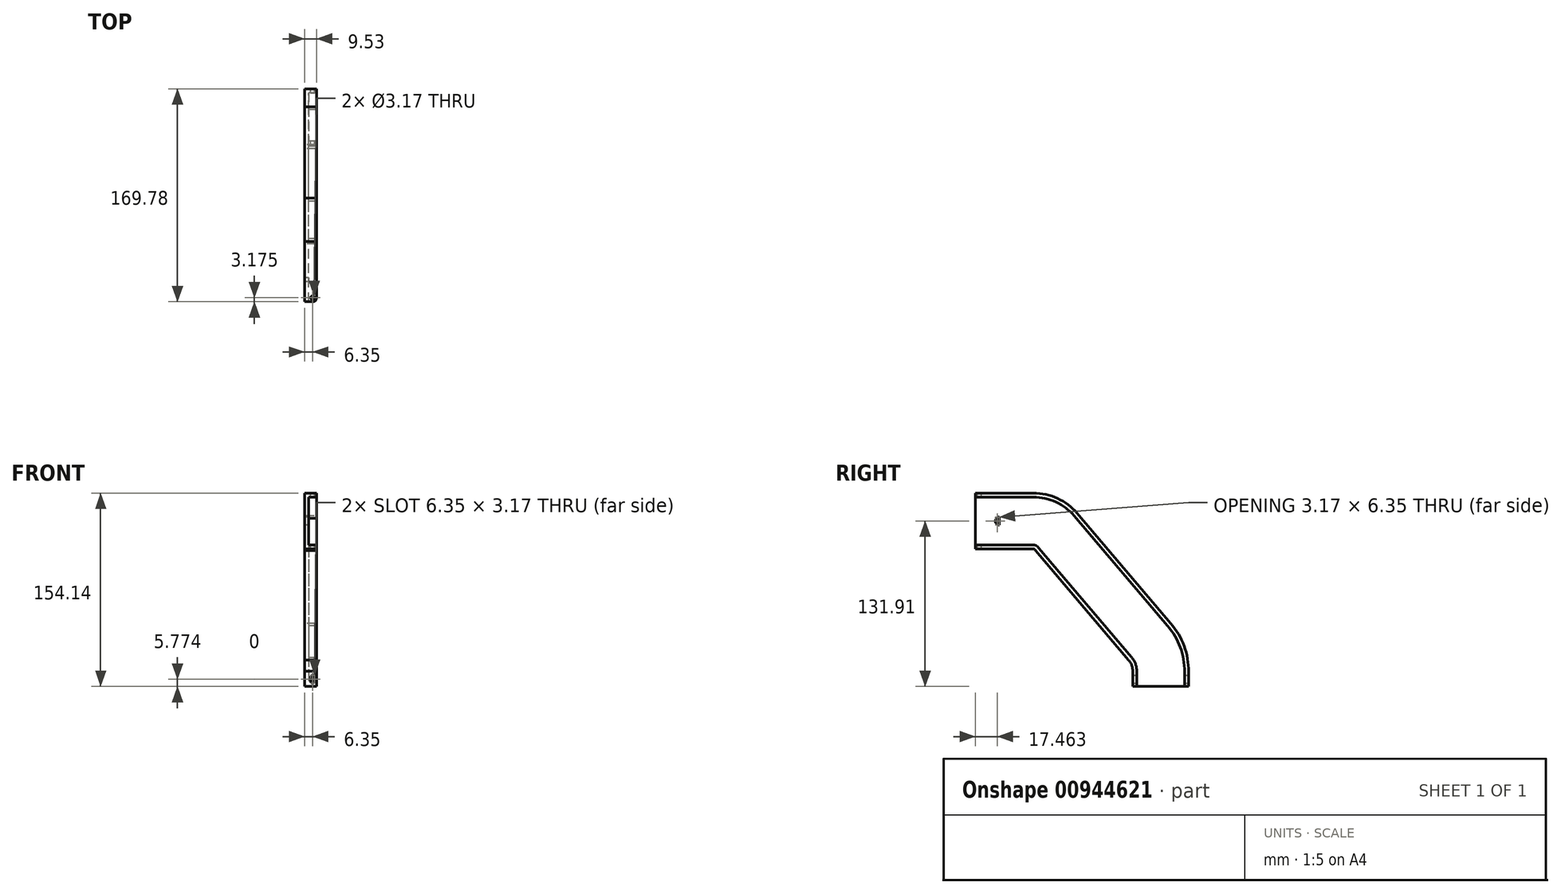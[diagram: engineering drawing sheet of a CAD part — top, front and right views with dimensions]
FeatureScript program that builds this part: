
annotation { "Feature Type Name" : "Feature", "Feature Type Description" : "" }
export const myFeature = defineFeature(function(context is Context, id is Id, definition is map)
    precondition{}
    {
        {
            var Q0;
            Q0=qCreatedBy(makeId("Front.planeOp"),FACE);
            var sketch = newSketch(context, id + "F0", { "sketchPlane" : qUnion([Q0])});
            skLineSegment(sketch, "E0.bottom", {"start": v(-3.18, 19.05) * mm, "end": v(3.18, 19.05) * mm});
            skLineSegment(sketch, "E0.top", {"start": v(-3.18, -19.05) * mm, "end": v(3.17, -19.05) * mm});
            skLineSegment(sketch, "E0.left", {"start": v(-3.18, 19.05) * mm, "end": v(-3.18, -19.05) * mm});
            skPoint(sketch, "E0.middle", {"position": v(0, 0) * mm});
            skLineSegment(sketch, "E1.0", {"start": v(-6.35, -22.22) * mm, "end": v(3.17, -22.22) * mm});
            skLineSegment(sketch, "E1.1", {"start": v(-6.35, 22.23) * mm, "end": v(-6.35, -22.23) * mm});
            skLineSegment(sketch, "E1.2", {"start": v(-6.35, 22.23) * mm, "end": v(3.18, 22.23) * mm});
            skLineSegment(sketch, "E2", {"start": v(3.18, 19.05) * mm, "end": v(3.18, 22.23) * mm});
            skLineSegment(sketch, "E3", {"start": v(3.17, -22.22) * mm, "end": v(3.17, -19.05) * mm});
            skSolve(sketch);
        }
        {
            var Q0;
            Q0 = qSketchRegion(id + "F0", true);
            extrude(context, id + "F1", {"entities" : qUnion([Q0]), "endBound" : BoundingType.SYMMETRIC, "depth" : 38.1 * mm, "offsetDistance" : 25.4 * mm});
        }
        {
            var Q0;
            Q0=makeQuery(id+"F1.opExtrude","SWEPT_FACE",FACE,{"disambiguationData":[OSD([sQuery(id+"F0.wireOp",EDGE,"E0.bottom")])]});
            var sketch = newSketch(context, id + "F2", { "sketchPlane" : qUnion([Q0])});
            skCircle(sketch, "E4", {"center": v(0, 15.88) * mm, "radius": 1.59 * mm});
            skPoint(sketch, "E4.centerSnap0", {"position": v(0, 19.05) * mm});
            skArc(sketch, "E5", {"start": v(3.18, 15.88) * mm, "mid": v(2.25, 18.12) * mm, "end": v(0, 19.05) * mm});
            skLineSegment(sketch, "E6", {"start": v(0, 19.05) * mm, "end": v(3.18, 19.05) * mm});
            skLineSegment(sketch, "E7", {"start": v(3.18, 15.88) * mm, "end": v(3.18, 19.05) * mm});
            skSolve(sketch);
        }
        {
            var Q0;
            Q0 = qSketchRegion(id + "F2", true);
            extrude(context, id + "F3", {"entities" : qUnion([Q0]), "operationType" : NewBodyOperationType.REMOVE, "endBound" : BoundingType.SYMMETRIC, "depth" : 209.9 * mm, "offsetDistance" : 25.4 * mm});
        }
        {
            var Q0;
            Q0=makeQuery(id+"F1.opExtrude","SWEPT_FACE",FACE,{"disambiguationData":[OSD([sQuery(id+"F0.wireOp",EDGE,"E1.1")])]});
            var sketch = newSketch(context, id + "F4", { "sketchPlane" : qUnion([Q0])});
            skPoint(sketch, "E8", {"position": v(0, 0) * mm});
            skSolve(sketch);
        }
        {
            var Q0;
            Q0=sQuery(id+"F4.wireOp",VERTEX,"E8");
            var Q1;
            Q1=makeQuery(id+"F1.opExtrude","SWEPT_BODY",BODY,{"disambiguationData":[OSD([sQuery(id+"F0.wireOp",EDGE,"E0.bottom"),sQuery(id+"F0.wireOp",EDGE,"E0.top"),sQuery(id+"F0.wireOp",EDGE,"E0.left"),sQuery(id+"F0.wireOp",EDGE,"E1.0"),sQuery(id+"F0.wireOp",EDGE,"E1.1"),sQuery(id+"F0.wireOp",EDGE,"E1.2"),sQuery(id+"F0.wireOp",EDGE,"E2"),sQuery(id+"F0.wireOp",EDGE,"E3")])]});
            hole(context, id + "F5", {"style" : HoleStyle.SIMPLE, "endStyle" : HoleEndStyle.BLIND, "holeDiameter" : 6.35 * mm, "majorDiameter" : 6.35 * mm, "holeDepth" : 12.7 * mm, "isTappedThrough" : true, "tappedDepth" : 12.7 * mm, "tapClearance" : 3, "startFromSketch" : true, "locations" : qUnion([Q0]), "scope" : qUnion([Q1])});
        }
        {
            var Q0;
            Q0=qCreatedBy(makeId("Right.planeOp"),FACE);
            var sketch = newSketch(context, id + "F6", { "sketchPlane" : qUnion([Q0])});
            skLineSegment(sketch, "E9.bottom", {"start": v(152.4, -114.3) * mm, "end": v(-152.4, -114.3) * mm});
            skLineSegment(sketch, "E9.top", {"start": v(152.4, 114.3) * mm, "end": v(-152.4, 114.3) * mm});
            skLineSegment(sketch, "E9.left", {"start": v(152.4, -114.3) * mm, "end": v(152.4, 114.3) * mm});
            skLineSegment(sketch, "E9.right", {"start": v(-152.4, -114.3) * mm, "end": v(-152.4, 114.3) * mm});
            skPoint(sketch, "E9.middle", {"position": v(0, 0) * mm});
            skSolve(sketch);
        }
        {
            var Q0;
            Q0=makeQuery(id+"F6.imprint","IMPRINT",FACE,{"disambiguationData":[TD([[makeQuery(id+"F6.imprint","IMPRINT",EDGE,{"derivedFrom":sQuery(id+"F6.wireOp",EDGE,"E9.bottom")}),-1.0]])]});
            var sketch = newSketch(context, id + "F7", { "sketchPlane" : qUnion([Q0])});
            skLineSegment(sketch, "E10", {"start": v(0, 0) * mm, "end": v(28.3, 0) * mm});
            skLineSegment(sketch, "E11", {"start": v(128.5, -120.1) * mm, "end": v(128.5, -131.91) * mm});
            skLineSegment(sketch, "E12", {"start": v(46.32, -9.68) * mm, "end": v(119.7, -96.15) * mm});
            skArc(sketch, "E13", {"start": v(46.32, -9.68) * mm, "mid": v(38.38, -2.86) * mm, "end": v(28.3, 0) * mm});
            skArc(sketch, "E14", {"start": v(128.5, -120.1) * mm, "mid": v(126.39, -107.29) * mm, "end": v(119.7, -96.15) * mm});
            skPoint(sketch, "E15.center.orphan", {"position": v(128.5, -106.51) * mm});
            skPoint(sketch, "E16.trimOffspring.start.orphan", {"position": v(128.5, -119.21) * mm});
            skSolve(sketch);
        }
        {
            var Q0;
            Q0=makeQuery(id+"F1.opExtrude","CAP_FACE",FACE,{"disambiguationData":[OSD([sQuery(id+"F0.wireOp",EDGE,"E0.bottom"),sQuery(id+"F0.wireOp",EDGE,"E0.top"),sQuery(id+"F0.wireOp",EDGE,"E0.left"),sQuery(id+"F0.wireOp",EDGE,"E1.0"),sQuery(id+"F0.wireOp",EDGE,"E1.1"),sQuery(id+"F0.wireOp",EDGE,"E1.2"),sQuery(id+"F0.wireOp",EDGE,"E2"),sQuery(id+"F0.wireOp",EDGE,"E3")])],"isStart":true});
            var Q1;
            Q1=sQuery(id+"F7.wireOp",EDGE,"E12");
            var Q2;
            Q2=sQuery(id+"F7.wireOp",EDGE,"E13");
            var Q3;
            Q3=sQuery(id+"F7.wireOp",EDGE,"E10");
            var Q4;
            Q4=sQuery(id+"F7.wireOp",EDGE,"E14");
            var Q5;
            Q5=sQuery(id+"F7.wireOp",EDGE,"E11");
            sweep(context, id + "F8", {"operationType" : NewBodyOperationType.ADD, "profiles" : qUnion([Q0]), "path" : qUnion([Q1, Q2, Q3, Q4, Q5])});
        }
        {
            var Q0;
            Q0=makeQuery(id+"F8.opSweep","SWEPT_FACE",FACE,{"disambiguationData":[OSD([sQuery(id+"F0.wireOp",EDGE,"E1.2"),sQuery(id+"F7.wireOp",EDGE,"E11")])]});
            var sketch = newSketch(context, id + "F9", { "sketchPlane" : qUnion([Q0])});
            skLineSegment(sketch, "E17.left", {"start": v(3.17, -127.72) * mm, "end": v(3.18, -124.55) * mm, "construction": true});
            skLineSegment(sketch, "E17.right", {"start": v(0, -127.72) * mm, "end": v(0, -124.55) * mm, "construction": true});
            skPoint(sketch, "E17.middle", {"position": v(1.59, -126.14) * mm});
            skPoint(sketch, "E17.middle.positionSnap0", {"position": v(-3.18, -126.14) * mm});
            skPoint(sketch, "E17.middle.positionSnap1", {"position": v(1.59, -131.91) * mm});
            skPoint(sketch, "E17.centerSnap0", {"position": v(-3.18, -126.14) * mm});
            skPoint(sketch, "E17.centerSnap1", {"position": v(1.59, -131.91) * mm});
            skArc(sketch, "E18", {"start": v(0, -127.72) * mm, "mid": v(1.59, -129.31) * mm, "end": v(3.17, -127.72) * mm, "construction": true});
            skArc(sketch, "E19", {"start": v(3.17, -124.55) * mm, "mid": v(1.59, -122.96) * mm, "end": v(0, -124.55) * mm, "construction": true});
            skArc(sketch, "E20", {"start": v(-1.59, -127.72) * mm, "mid": v(0, -129.31) * mm, "end": v(1.59, -127.72) * mm});
            skArc(sketch, "E21", {"start": v(1.59, -124.55) * mm, "mid": v(0, -122.96) * mm, "end": v(-1.59, -124.55) * mm});
            skLineSegment(sketch, "E22", {"start": v(1.59, -124.55) * mm, "end": v(1.59, -127.72) * mm});
            skLineSegment(sketch, "E23", {"start": v(-1.59, -127.72) * mm, "end": v(-1.59, -124.55) * mm});
            skSolve(sketch);
        }
        {
            var Q0;
            Q0=makeQuery(id+"F9.imprint","IMPRINT",FACE,{"disambiguationData":[TD([[makeQuery(id+"F9.imprint","IMPRINT",EDGE,{"derivedFrom":sQuery(id+"F9.wireOp",EDGE,"E20")}),1.0]])]});
            extrude(context, id + "F10", {"entities" : qUnion([Q0]), "operationType" : NewBodyOperationType.REMOVE, "endBound" : BoundingType.THROUGH_ALL, "oppositeDirection" : true, "depth" : 25.4 * mm, "offsetDistance" : 25.4 * mm});
        }
    });
